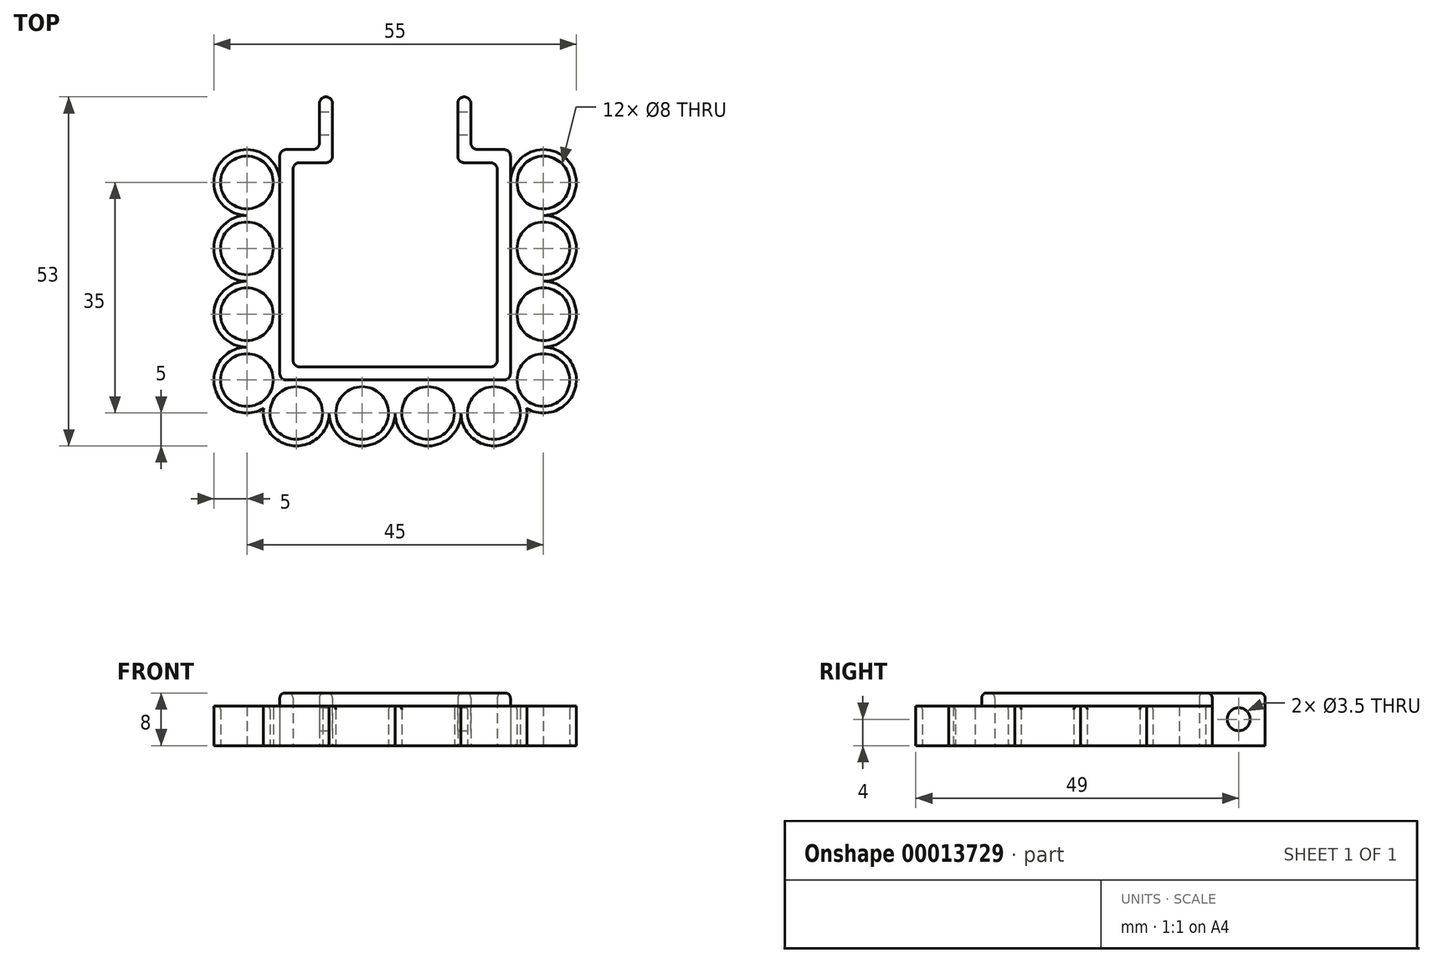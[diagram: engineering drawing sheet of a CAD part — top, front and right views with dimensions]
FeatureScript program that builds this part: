
annotation { "Feature Type Name" : "Feature", "Feature Type Description" : "" }
export const myFeature = defineFeature(function(context is Context, id is Id, definition is map)
    precondition{}
    {
        {
            var Q0;
            Q0=qCreatedBy(makeId("Top.planeOp"),FACE);
            var sketch = newSketch(context, id + "F0", { "sketchPlane" : qUnion([Q0])});
            skLineSegment(sketch, "E0.rect.bottom", {"start": v(15.5, -15.5) * mm, "end": v(-15.5, -15.5) * mm});
            skLineSegment(sketch, "E0.rect.top", {"start": v(15.5, 15.5) * mm, "end": v(-15.5, 15.5) * mm});
            skLineSegment(sketch, "E0.rect.left", {"start": v(15.5, -15.5) * mm, "end": v(15.5, 15.5) * mm});
            skLineSegment(sketch, "E0.rect.right", {"start": v(-15.5, -15.5) * mm, "end": v(-15.5, 15.5) * mm});
            skPoint(sketch, "E0.rect.middle", {"position": v(0, 0) * mm});
            skLineSegment(sketch, "E1.rect.bottom", {"start": v(17.5, 17.5) * mm, "end": v(-17.5, 17.5) * mm});
            skLineSegment(sketch, "E1.rect.top", {"start": v(17.5, -17.5) * mm, "end": v(-17.5, -17.5) * mm});
            skLineSegment(sketch, "E1.rect.left", {"start": v(17.5, 17.5) * mm, "end": v(17.5, -17.5) * mm});
            skLineSegment(sketch, "E1.rect.right", {"start": v(-17.5, 17.5) * mm, "end": v(-17.5, -17.5) * mm});
            skLineSegment(sketch, "E2", {"start": v(-9.5, 25.5) * mm, "end": v(-9.5, 15.5) * mm});
            skLineSegment(sketch, "E3", {"start": v(9.5, 25.5) * mm, "end": v(9.5, 15.5) * mm});
            skLineSegment(sketch, "E4", {"start": v(-11.5, 17.5) * mm, "end": v(-11.5, 25.5) * mm});
            skLineSegment(sketch, "E5", {"start": v(-11.5, 25.5) * mm, "end": v(-9.5, 25.5) * mm});
            skLineSegment(sketch, "E6", {"start": v(11.5, 17.5) * mm, "end": v(11.5, 25.5) * mm});
            skLineSegment(sketch, "E7", {"start": v(11.5, 25.5) * mm, "end": v(9.5, 25.5) * mm});
            skPoint(sketch, "E8.orphan", {"position": v(-9.5, 17.5) * mm});
            skSolve(sketch);
        }
        {
            var Q0;
            {var subQ1=sQuery(id+"F0.wireOp",EDGE,"E4");Q0=makeQuery(id+"F0.imprint","IMPRINT",FACE,{"disambiguationData":[TD([[makeQuery(id+"F0.imprint","IMPRINT",EDGE,{"derivedFrom":subQ1}),-1.0]])]});}
            var Q1;
            Q1=makeQuery(id+"F0.imprint","IMPRINT",FACE,{"disambiguationData":[TD([[makeQuery(id+"F0.imprint","IMPRINT",EDGE,{"derivedFrom":sQuery(id+"F0.wireOp",EDGE,"E0.rect.bottom")}),1.0]])]});
            var Q2;
            {var subQ1=sQuery(id+"F0.wireOp",EDGE,"E6");Q2=makeQuery(id+"F0.imprint","IMPRINT",FACE,{"disambiguationData":[TD([[makeQuery(id+"F0.imprint","IMPRINT",EDGE,{"derivedFrom":subQ1}),1.0]])]});}
            extrude(context, id + "F1", {"entities" : qUnion([Q0, Q1, Q2]), "depth" : 8 * mm});
        }
        {
            var Q0;
            Q0=qCreatedBy(makeId("Top.planeOp"),FACE);
            var sketch = newSketch(context, id + "F2", { "sketchPlane" : qUnion([Q0])});
            skLineSegment(sketch, "E9.0.0", {"start": v(-11.5, 17.5) * mm, "end": v(-11.5, 25.5) * mm});
            skLineSegment(sketch, "E9.0.1", {"start": v(-11.5, 25.5) * mm, "end": v(-9.5, 25.5) * mm});
            skLineSegment(sketch, "E9.0.2", {"start": v(-9.5, 25.5) * mm, "end": v(-9.5, 15.5) * mm});
            skLineSegment(sketch, "E9.0.3", {"start": v(-9.5, 15.5) * mm, "end": v(-15.5, 15.5) * mm});
            skLineSegment(sketch, "E9.0.4", {"start": v(-15.5, -15.5) * mm, "end": v(-15.5, 15.5) * mm});
            skLineSegment(sketch, "E9.0.5", {"start": v(15.5, -15.5) * mm, "end": v(-15.5, -15.5) * mm});
            skLineSegment(sketch, "E9.0.6", {"start": v(15.5, -15.5) * mm, "end": v(15.5, 15.5) * mm});
            skLineSegment(sketch, "E9.0.7", {"start": v(15.5, 15.5) * mm, "end": v(9.5, 15.5) * mm});
            skLineSegment(sketch, "E9.0.8", {"start": v(9.5, 25.5) * mm, "end": v(9.5, 15.5) * mm});
            skLineSegment(sketch, "E9.0.9", {"start": v(11.5, 25.5) * mm, "end": v(9.5, 25.5) * mm});
            skLineSegment(sketch, "E9.0.10", {"start": v(11.5, 17.5) * mm, "end": v(11.5, 25.5) * mm});
            skLineSegment(sketch, "E9.0.11", {"start": v(17.5, 17.5) * mm, "end": v(11.5, 17.5) * mm});
            skLineSegment(sketch, "E9.0.12", {"start": v(17.5, 17.5) * mm, "end": v(17.5, -17.5) * mm});
            skLineSegment(sketch, "E9.0.13", {"start": v(17.5, -17.5) * mm, "end": v(-17.5, -17.5) * mm});
            skLineSegment(sketch, "E9.0.14", {"start": v(-17.5, 17.5) * mm, "end": v(-17.5, -17.5) * mm});
            skLineSegment(sketch, "E9.0.15", {"start": v(-11.5, 17.5) * mm, "end": v(-17.5, 17.5) * mm});
            skLineSegment(sketch, "E10", {"start": v(-17.5, 17.5) * mm, "end": v(-27.5, 17.5) * mm, "construction": true});
            skLineSegment(sketch, "E11", {"start": v(-27.5, 17.5) * mm, "end": v(-27.5, -27.5) * mm, "construction": true});
            skLineSegment(sketch, "E12", {"start": v(-27.5, -27.5) * mm, "end": v(27.5, -27.5) * mm, "construction": true});
            skLineSegment(sketch, "E13", {"start": v(27.5, -27.5) * mm, "end": v(27.5, 17.5) * mm, "construction": true});
            skLineSegment(sketch, "E14", {"start": v(27.5, 17.5) * mm, "end": v(17.5, 17.5) * mm, "construction": true});
            skLineSegment(sketch, "E15", {"start": v(-22.5, -22.5) * mm, "end": v(22.5, -22.5) * mm, "construction": true});
            skLineSegment(sketch, "E16", {"start": v(22.5, 17.5) * mm, "end": v(22.5, -22.5) * mm, "construction": true});
            skCircle(sketch, "E17", {"center": v(-22.5, 12.5) * mm, "radius": 4 * mm});
            skCircle(sketch, "E18", {"center": v(-22.5, 2.5) * mm, "radius": 4 * mm});
            skCircle(sketch, "E19", {"center": v(-22.5, -7.5) * mm, "radius": 4 * mm});
            skCircle(sketch, "E20", {"center": v(22.5, 12.5) * mm, "radius": 4 * mm});
            skCircle(sketch, "E21", {"center": v(22.5, 2.5) * mm, "radius": 4 * mm});
            skCircle(sketch, "E22", {"center": v(22.5, -7.5) * mm, "radius": 4 * mm});
            skLineSegment(sketch, "E23", {"start": v(-22.5, 17.5) * mm, "end": v(-22.5, -22.5) * mm, "construction": true});
            skCircle(sketch, "E24", {"center": v(-15, -22.5) * mm, "radius": 4 * mm});
            skCircle(sketch, "E25", {"center": v(5, -22.5) * mm, "radius": 4 * mm});
            skCircle(sketch, "E26", {"center": v(-5, -22.5) * mm, "radius": 4 * mm});
            skCircle(sketch, "E27", {"center": v(-22.5, -17.5) * mm, "radius": 4 * mm});
            skCircle(sketch, "E28", {"center": v(22.5, -17.5) * mm, "radius": 4 * mm});
            skCircle(sketch, "E29", {"center": v(15, -22.5) * mm, "radius": 4 * mm});
            skArc(sketch, "E30", {"start": v(-17.5, 12.5) * mm, "mid": v(-26.04, 16.04) * mm, "end": v(-22.5, 7.5) * mm});
            skArc(sketch, "E31", {"start": v(-17.5, 2.5) * mm, "mid": v(-26.04, 6.04) * mm, "end": v(-22.5, -2.5) * mm});
            skArc(sketch, "E32", {"start": v(-17.5, -7.5) * mm, "mid": v(-26.04, -3.96) * mm, "end": v(-22.5, -12.5) * mm});
            skArc(sketch, "E33", {"start": v(-17.55, -18.2) * mm, "mid": v(-26.66, -14.73) * mm, "end": v(-19.95, -21.8) * mm});
            skArc(sketch, "E34", {"start": v(-19.95, -21.8) * mm, "mid": v(-15.35, -27.49) * mm, "end": v(-10, -22.5) * mm});
            skArc(sketch, "E35", {"start": v(-5, -17.5) * mm, "mid": v(-8.54, -26.04) * mm, "end": v(0, -22.5) * mm});
            skArc(sketch, "E36", {"start": v(0, -22.5) * mm, "mid": v(8.54, -26.04) * mm, "end": v(5, -17.5) * mm});
            skArc(sketch, "E37", {"start": v(10, -22.5) * mm, "mid": v(15.35, -27.49) * mm, "end": v(19.95, -21.8) * mm});
            skArc(sketch, "E38", {"start": v(19.95, -21.8) * mm, "mid": v(26.66, -14.73) * mm, "end": v(17.55, -18.2) * mm});
            skArc(sketch, "E39", {"start": v(22.5, -12.5) * mm, "mid": v(26.04, -3.96) * mm, "end": v(17.5, -7.5) * mm});
            skArc(sketch, "E40", {"start": v(22.5, -2.5) * mm, "mid": v(26.04, 6.04) * mm, "end": v(17.5, 2.5) * mm});
            skArc(sketch, "E41", {"start": v(22.5, 7.5) * mm, "mid": v(26.04, 16.04) * mm, "end": v(17.5, 12.5) * mm});
            skSolve(sketch);
        }
        {
            var Q0;
            Q0=makeQuery(id+"F2.imprint","IMPRINT",FACE,{"disambiguationData":[TD([[makeQuery(id+"F2.imprint","IMPRINT",EDGE,{"derivedFrom":sQuery(id+"F2.wireOp",EDGE,"E20")}),-1.0]])]});
            var Q1;
            Q1=makeQuery(id+"F2.imprint","IMPRINT",FACE,{"disambiguationData":[TD([[makeQuery(id+"F2.imprint","IMPRINT",EDGE,{"derivedFrom":sQuery(id+"F2.wireOp",EDGE,"E21")}),-1.0]])]});
            var Q2;
            Q2=makeQuery(id+"F2.imprint","IMPRINT",FACE,{"disambiguationData":[TD([[makeQuery(id+"F2.imprint","IMPRINT",EDGE,{"derivedFrom":sQuery(id+"F2.wireOp",EDGE,"E17")}),-1.0]])]});
            var Q3;
            Q3=makeQuery(id+"F2.imprint","IMPRINT",FACE,{"disambiguationData":[TD([[makeQuery(id+"F2.imprint","IMPRINT",EDGE,{"derivedFrom":sQuery(id+"F2.wireOp",EDGE,"E18")}),-1.0]])]});
            var Q4;
            Q4=makeQuery(id+"F2.imprint","IMPRINT",FACE,{"disambiguationData":[TD([[makeQuery(id+"F2.imprint","IMPRINT",EDGE,{"derivedFrom":sQuery(id+"F2.wireOp",EDGE,"E19")}),-1.0]])]});
            var Q5;
            Q5=makeQuery(id+"F2.imprint","IMPRINT",FACE,{"disambiguationData":[TD([[makeQuery(id+"F2.imprint","IMPRINT",EDGE,{"derivedFrom":sQuery(id+"F2.wireOp",EDGE,"E24")}),-1.0]])]});
            var Q6;
            Q6=makeQuery(id+"F2.imprint","IMPRINT",FACE,{"disambiguationData":[TD([[makeQuery(id+"F2.imprint","IMPRINT",EDGE,{"derivedFrom":sQuery(id+"F2.wireOp",EDGE,"E22")}),-1.0]])]});
            var Q7;
            Q7=makeQuery(id+"F2.imprint","IMPRINT",FACE,{"disambiguationData":[TD([[makeQuery(id+"F2.imprint","IMPRINT",EDGE,{"derivedFrom":sQuery(id+"F2.wireOp",EDGE,"E28")}),-1.0]])]});
            var Q8;
            Q8=makeQuery(id+"F2.imprint","IMPRINT",FACE,{"disambiguationData":[TD([[makeQuery(id+"F2.imprint","IMPRINT",EDGE,{"derivedFrom":sQuery(id+"F2.wireOp",EDGE,"E25")}),-1.0]])]});
            extrude(context, id + "F3", {"entities" : qUnion([Q0, Q1, Q2, Q3, Q4, Q5, Q6, Q7, Q8]), "operationType" : NewBodyOperationType.ADD, "depth" : 6 * mm});
        }
        {
            var Q0;
            Q0=makeQuery(id+"F1.opExtrude","SWEPT_FACE",FACE,{"disambiguationData":[OSD([sQuery(id+"F0.wireOp",EDGE,"E6")])]});
            var sketch = newSketch(context, id + "F4", { "sketchPlane" : qUnion([Q0])});
            skLineSegment(sketch, "E42", {"start": v(21.5, 8) * mm, "end": v(21.5, 0) * mm, "construction": true});
            skCircle(sketch, "E43", {"center": v(21.5, 4) * mm, "radius": 1.75 * mm});
            skSolve(sketch);
        }
        {
            var Q0;
            Q0=makeQuery(id+"F4.imprint","IMPRINT",FACE,{"disambiguationData":[TD([[makeQuery(id+"F4.imprint","IMPRINT",EDGE,{"derivedFrom":sQuery(id+"F4.wireOp",EDGE,"E43")}),1.0]])]});
            extrude(context, id + "F5", {"entities" : qUnion([Q0]), "operationType" : NewBodyOperationType.REMOVE, "endBound" : BoundingType.THROUGH_ALL, "oppositeDirection" : true, "depth" : 100 * mm});
        }
        {
            var Q0;
            Q0=makeQuery(id+"F1.opExtrude","SWEPT_EDGE",EDGE,{"disambiguationData":[OSD([sQuery(id+"F0.wireOp",EDGE,"E6"),sQuery(id+"F0.wireOp",EDGE,"E7")])]});
            var Q1;
            Q1=makeQuery(id+"F1.opExtrude","SWEPT_EDGE",EDGE,{"disambiguationData":[OSD([sQuery(id+"F0.wireOp",EDGE,"E1.rect.bottom"),sQuery(id+"F0.wireOp",EDGE,"E6")])]});
            var Q2;
            Q2=makeQuery(id+"F1.opExtrude","SWEPT_EDGE",EDGE,{"disambiguationData":[OSD([sQuery(id+"F0.wireOp",EDGE,"E1.rect.bottom"),sQuery(id+"F0.wireOp",EDGE,"E1.rect.left")])]});
            var Q3;
            Q3=makeQuery(id+"F1.opExtrude","SWEPT_EDGE",EDGE,{"disambiguationData":[OSD([sQuery(id+"F0.wireOp",EDGE,"E2"),sQuery(id+"F0.wireOp",EDGE,"E5")])]});
            var Q4;
            Q4=makeQuery(id+"F1.opExtrude","SWEPT_EDGE",EDGE,{"disambiguationData":[OSD([sQuery(id+"F0.wireOp",EDGE,"E3"),sQuery(id+"F0.wireOp",EDGE,"E7")])]});
            var Q5;
            Q5=makeQuery(id+"F1.opExtrude","SWEPT_EDGE",EDGE,{"disambiguationData":[OSD([sQuery(id+"F0.wireOp",EDGE,"E4"),sQuery(id+"F0.wireOp",EDGE,"E5")])]});
            var Q6;
            Q6=makeQuery(id+"F1.opExtrude","SWEPT_EDGE",EDGE,{"disambiguationData":[OSD([sQuery(id+"F0.wireOp",EDGE,"E1.rect.bottom"),sQuery(id+"F0.wireOp",EDGE,"E1.rect.right")])]});
            var Q7;
            Q7=makeQuery(id+"F1.opExtrude","SWEPT_EDGE",EDGE,{"disambiguationData":[OSD([sQuery(id+"F0.wireOp",EDGE,"E1.rect.bottom"),sQuery(id+"F0.wireOp",EDGE,"E4")])]});
            var Q8;
            Q8=makeQuery(id+"F1.opExtrude","SWEPT_EDGE",EDGE,{"disambiguationData":[OSD([sQuery(id+"F0.wireOp",EDGE,"E0.rect.top"),sQuery(id+"F0.wireOp",EDGE,"E2")])]});
            var Q9;
            Q9=makeQuery(id+"F1.opExtrude","SWEPT_EDGE",EDGE,{"disambiguationData":[OSD([sQuery(id+"F0.wireOp",EDGE,"E0.rect.top"),sQuery(id+"F0.wireOp",EDGE,"E3")])]});
            var Q10;
            Q10=makeQuery(id+"F1.opExtrude","SWEPT_EDGE",EDGE,{"disambiguationData":[OSD([sQuery(id+"F0.wireOp",EDGE,"E0.rect.top"),sQuery(id+"F0.wireOp",EDGE,"E0.rect.left")])]});
            var Q11;
            Q11=makeQuery(id+"F1.opExtrude","SWEPT_EDGE",EDGE,{"disambiguationData":[OSD([sQuery(id+"F0.wireOp",EDGE,"E0.rect.bottom"),sQuery(id+"F0.wireOp",EDGE,"E0.rect.left")])]});
            var Q12;
            Q12=makeQuery(id+"F1.opExtrude","SWEPT_EDGE",EDGE,{"disambiguationData":[OSD([sQuery(id+"F0.wireOp",EDGE,"E0.rect.bottom"),sQuery(id+"F0.wireOp",EDGE,"E0.rect.right")])]});
            var Q13;
            Q13=makeQuery(id+"F1.opExtrude","SWEPT_EDGE",EDGE,{"disambiguationData":[OSD([sQuery(id+"F0.wireOp",EDGE,"E0.rect.top"),sQuery(id+"F0.wireOp",EDGE,"E0.rect.right")])]});
            var Q14;
            Q14=makeQuery(id+"F1.opExtrude","SWEPT_EDGE",EDGE,{"disambiguationData":[OSD([sQuery(id+"F0.wireOp",EDGE,"E1.rect.top"),sQuery(id+"F0.wireOp",EDGE,"E1.rect.right")])]});
            var Q15;
            Q15=makeQuery(id+"F1.opExtrude","SWEPT_EDGE",EDGE,{"disambiguationData":[OSD([sQuery(id+"F0.wireOp",EDGE,"E1.rect.top"),sQuery(id+"F0.wireOp",EDGE,"E1.rect.left")])]});
            fillet(context, id + "F6", {"entities" : qUnion([Q0, Q1, Q2, Q3, Q4, Q5, Q6, Q7, Q8, Q9, Q10, Q11, Q12, Q13, Q14, Q15]), "radius" : 1 * mm, "tangentPropagation" : true, "allowEdgeOverflow" : false});
        }
        {
            var Q0;
            Q0=makeQuery(id+"F1.opExtrude","CAP_EDGE",EDGE,{"disambiguationData":[OSD([sQuery(id+"F0.wireOp",EDGE,"E1.rect.top")])],"isStart":false});
            fillet(context, id + "F7", {"entities" : qUnion([Q0]), "radius" : 0.8 * mm, "tangentPropagation" : true, "allowEdgeOverflow" : false});
        }
        {
            var Q0;
            Q0=makeQuery(id+"F3.opExtrude","CAP_EDGE",EDGE,{"disambiguationData":[OSD([sQuery(id+"F2.wireOp",EDGE,"E20")])],"isStart":false});
            var Q1;
            Q1=makeQuery(id+"F3.opExtrude","CAP_EDGE",EDGE,{"disambiguationData":[OSD([sQuery(id+"F2.wireOp",EDGE,"E21")])],"isStart":false});
            var Q2;
            Q2=makeQuery(id+"F3.opExtrude","CAP_EDGE",EDGE,{"disambiguationData":[OSD([sQuery(id+"F2.wireOp",EDGE,"E22")])],"isStart":false});
            var Q3;
            Q3=makeQuery(id+"F3.opExtrude","SWEPT_FACE",FACE,{"disambiguationData":[OSD([sQuery(id+"F2.wireOp",EDGE,"E28")])]});
            var Q4;
            Q4=makeQuery(id+"F3.opExtrude","CAP_EDGE",EDGE,{"disambiguationData":[OSD([sQuery(id+"F2.wireOp",EDGE,"E29")])],"isStart":false});
            var Q5;
            Q5=makeQuery(id+"F3.opExtrude","CAP_EDGE",EDGE,{"disambiguationData":[OSD([sQuery(id+"F2.wireOp",EDGE,"E25")])],"isStart":false});
            var Q6;
            Q6=makeQuery(id+"F3.opExtrude","CAP_EDGE",EDGE,{"disambiguationData":[OSD([sQuery(id+"F2.wireOp",EDGE,"E26")])],"isStart":false});
            var Q7;
            Q7=makeQuery(id+"F3.opExtrude","CAP_EDGE",EDGE,{"disambiguationData":[OSD([sQuery(id+"F2.wireOp",EDGE,"E24")])],"isStart":false});
            var Q8;
            Q8=makeQuery(id+"F3.opExtrude","CAP_EDGE",EDGE,{"disambiguationData":[OSD([sQuery(id+"F2.wireOp",EDGE,"E27")])],"isStart":false});
            var Q9;
            Q9=makeQuery(id+"F3.opExtrude","CAP_EDGE",EDGE,{"disambiguationData":[OSD([sQuery(id+"F2.wireOp",EDGE,"E19")])],"isStart":false});
            var Q10;
            Q10=makeQuery(id+"F3.opExtrude","CAP_EDGE",EDGE,{"disambiguationData":[OSD([sQuery(id+"F2.wireOp",EDGE,"E18")])],"isStart":false});
            var Q11;
            Q11=makeQuery(id+"F3.opExtrude","CAP_EDGE",EDGE,{"disambiguationData":[OSD([sQuery(id+"F2.wireOp",EDGE,"E17")])],"isStart":false});
            fillet(context, id + "F8", {"entities" : qUnion([Q0, Q1, Q2, Q3, Q4, Q5, Q6, Q7, Q8, Q9, Q10, Q11]), "radius" : 0.5 * mm, "tangentPropagation" : true, "allowEdgeOverflow" : false});
        }
    });
